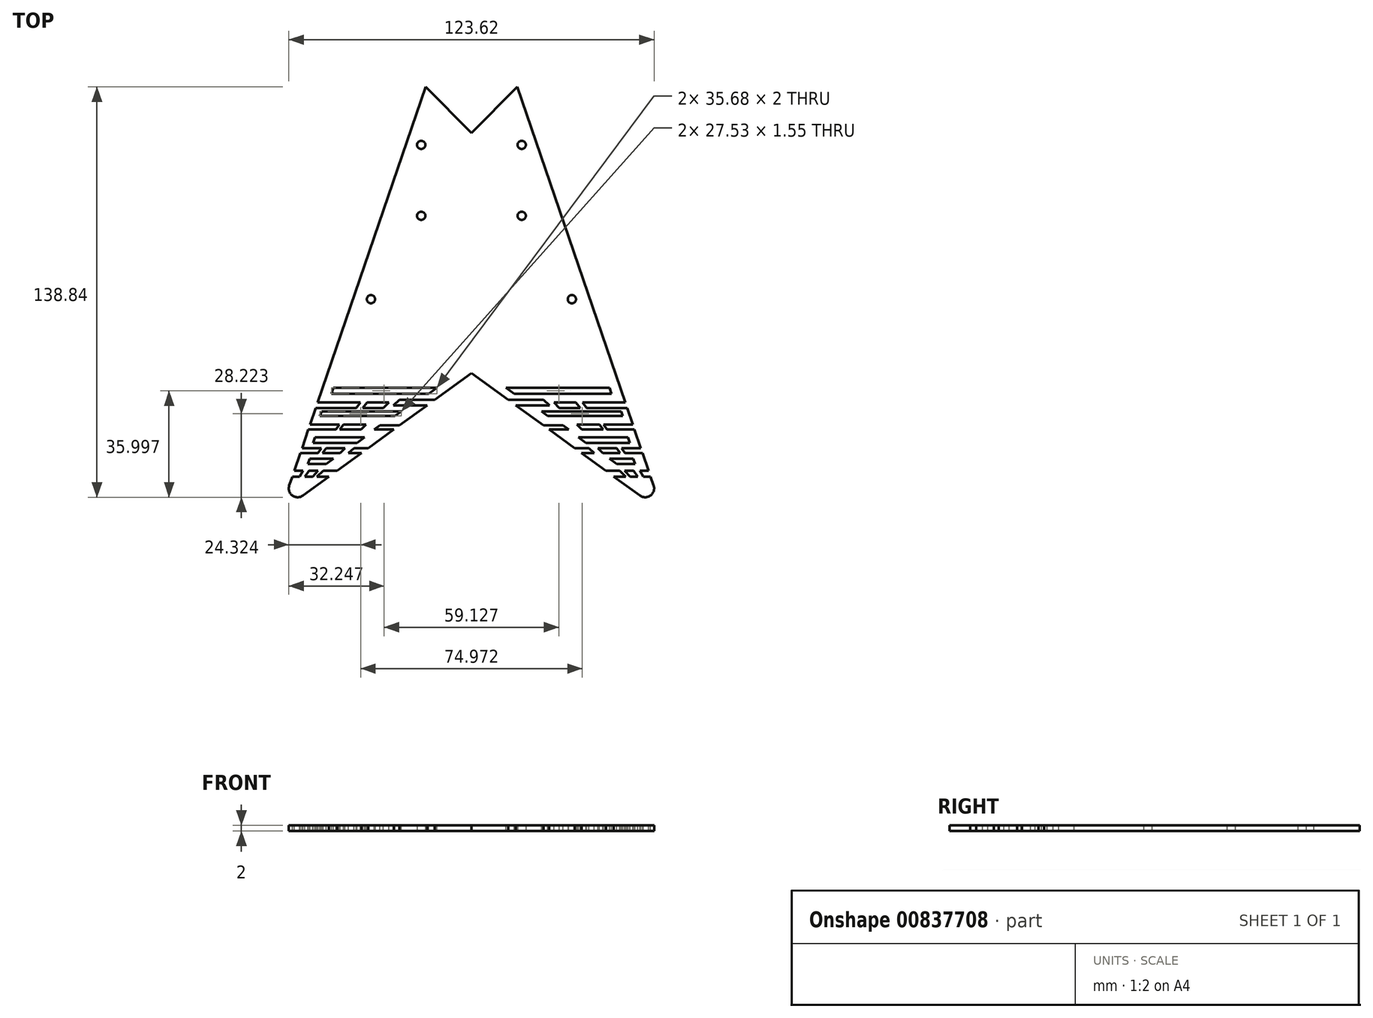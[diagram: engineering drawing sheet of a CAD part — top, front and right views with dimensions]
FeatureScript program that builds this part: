
annotation { "Feature Type Name" : "Feature", "Feature Type Description" : "" }
export const myFeature = defineFeature(function(context is Context, id is Id, definition is map)
    precondition{}
    {
        {
            var Q0;
            Q0=qCreatedBy(makeId("Top.planeOp"),FACE);
            var sketch = newSketch(context, id + "F0", { "sketchPlane" : qUnion([Q0])});
            skLineSegment(sketch, "E0", {"start": v(0, 142.22) * mm, "end": v(-64.72, -47.02) * mm});
            skLineSegment(sketch, "E1", {"start": v(-64.72, -47.02) * mm, "end": v(0, 0) * mm});
            skLineSegment(sketch, "E2.MirrorCS", {"start": v(0, 142.22) * mm, "end": v(64.72, -47.02) * mm});
            skLineSegment(sketch, "E3.MirrorCS", {"start": v(64.72, -47.02) * mm, "end": v(0, 0) * mm});
            skCircle(sketch, "E4", {"center": v(-17, 77.22) * mm, "radius": 1.4 * mm});
            skCircle(sketch, "E5", {"center": v(-17, 53.22) * mm, "radius": 1.4 * mm});
            skCircle(sketch, "E6.MirrorC", {"center": v(17, 77.22) * mm, "radius": 1.4 * mm});
            skCircle(sketch, "E7.MirrorC", {"center": v(17, 53.22) * mm, "radius": 1.4 * mm});
            skCircle(sketch, "E8", {"center": v(-34, 25) * mm, "radius": 1.4 * mm});
            skCircle(sketch, "E9.MirrorC", {"center": v(34, 25) * mm, "radius": 1.4 * mm});
            skSolve(sketch);
        }
        {
            var Q0;
            Q0 = qSketchRegion(id + "F0", true);
            extrude(context, id + "F1", {"entities" : qUnion([Q0]), "depth" : 2 * mm, "offsetDistance" : 25 * mm});
        }
        {
            var Q0;
            Q0=makeQuery(id+"F1.opExtrude","CAP_FACE",FACE,{"disambiguationData":[OSD([sQuery(id+"F0.wireOp",EDGE,"E0"),sQuery(id+"F0.wireOp",EDGE,"E1"),sQuery(id+"F0.wireOp",EDGE,"E2.MirrorCS"),sQuery(id+"F0.wireOp",EDGE,"E3.MirrorCS"),sQuery(id+"F0.wireOp",EDGE,"E4"),sQuery(id+"F0.wireOp",EDGE,"E5"),sQuery(id+"F0.wireOp",EDGE,"E6.MirrorC"),sQuery(id+"F0.wireOp",EDGE,"E7.MirrorC"),sQuery(id+"F0.wireOp",EDGE,"gKl59jUD-f7xt-qJ04-XvQ7-xEkOoHtsUVjT"),sQuery(id+"F0.wireOp",EDGE,"E8"),sQuery(id+"F0.wireOp",EDGE,"E9.MirrorC")])],"isStart":false});
            var sketch = newSketch(context, id + "F2", { "sketchPlane" : qUnion([Q0])});
            skLineSegment(sketch, "E10.bottom", {"start": v(-46.72, -5.02) * mm, "end": v(-11.72, -5.02) * mm});
            skLineSegment(sketch, "E11.bottom", {"start": v(-24.42, -9.02) * mm, "end": v(-12.42, -9.02) * mm});
            skLineSegment(sketch, "E12.bottom", {"start": v(-50.72, -13.02) * mm, "end": v(-23.72, -13.02) * mm});
            skLineSegment(sketch, "E13.bottom", {"start": v(-55.18, -19.11) * mm, "end": v(-45.87, -19.11) * mm});
            skLineSegment(sketch, "E14.bottom", {"start": v(-52.95, -21.77) * mm, "end": v(-36.18, -21.77) * mm});
            skLineSegment(sketch, "E15.bottom", {"start": v(-57.88, -27.02) * mm, "end": v(-51.93, -27.1) * mm});
            skLineSegment(sketch, "E16.bottom", {"start": v(-49.2, -25.4) * mm, "end": v(-42.82, -25.4) * mm});
            skLineSegment(sketch, "E17.bottom", {"start": v(-39.7, -25.4) * mm, "end": v(-34.96, -25.4) * mm});
            skLineSegment(sketch, "E18.bottom", {"start": v(-54.72, -29.02) * mm, "end": v(-46.72, -29.02) * mm});
            skLineSegment(sketch, "E19", {"start": v(-60.62, -35.02) * mm, "end": v(-59.93, -33.02) * mm});
            skLineSegment(sketch, "E20", {"start": v(-46.72, -5.02) * mm, "end": v(-47.4, -7.02) * mm});
            skLineSegment(sketch, "E21", {"start": v(-11.72, -5.02) * mm, "end": v(-14.47, -7.02) * mm});
            skLineSegment(sketch, "E22", {"start": v(-14.47, -7.02) * mm, "end": v(-47.4, -7.02) * mm});
            skLineSegment(sketch, "E23", {"start": v(-52.7, -11.87) * mm, "end": v(-52.05, -9.98) * mm});
            skLineSegment(sketch, "E24", {"start": v(-52.05, -9.98) * mm, "end": v(-37.59, -9.98) * mm});
            skLineSegment(sketch, "E25", {"start": v(-37.59, -9.98) * mm, "end": v(-38.97, -11.87) * mm});
            skLineSegment(sketch, "E26", {"start": v(-24.42, -9.02) * mm, "end": v(-26.42, -10.9) * mm});
            skLineSegment(sketch, "E27", {"start": v(-26.42, -10.9) * mm, "end": v(-15.02, -10.9) * mm});
            skLineSegment(sketch, "E28", {"start": v(-15.02, -10.9) * mm, "end": v(-12.42, -9.02) * mm});
            skLineSegment(sketch, "E29", {"start": v(-52.7, -11.87) * mm, "end": v(-38.97, -11.87) * mm});
            skLineSegment(sketch, "E30", {"start": v(-50.72, -13.02) * mm, "end": v(-51.25, -14.57) * mm});
            skLineSegment(sketch, "E31", {"start": v(-51.25, -14.57) * mm, "end": v(-25.85, -14.57) * mm});
            skLineSegment(sketch, "E32", {"start": v(-25.85, -14.57) * mm, "end": v(-23.72, -13.02) * mm});
            skLineSegment(sketch, "E33", {"start": v(-54.6, -17.46) * mm, "end": v(-44.75, -17.46) * mm});
            skLineSegment(sketch, "E34", {"start": v(-44.75, -17.46) * mm, "end": v(-45.87, -19.11) * mm});
            skLineSegment(sketch, "E35", {"start": v(-26.3, -19.11) * mm, "end": v(-24.37, -17.7) * mm});
            skLineSegment(sketch, "E36", {"start": v(-43.33, -17.44) * mm, "end": v(-35.64, -17.44) * mm});
            skLineSegment(sketch, "E37", {"start": v(-35.64, -17.44) * mm, "end": v(-37.29, -19.11) * mm});
            skLineSegment(sketch, "E38", {"start": v(-37.29, -19.11) * mm, "end": v(-44.54, -19.11) * mm});
            skLineSegment(sketch, "E39", {"start": v(-44.54, -19.11) * mm, "end": v(-43.33, -17.44) * mm});
            skLineSegment(sketch, "E40", {"start": v(-52.95, -21.77) * mm, "end": v(-53.6, -23.66) * mm});
            skLineSegment(sketch, "E41", {"start": v(-53.6, -23.66) * mm, "end": v(-38.79, -23.66) * mm});
            skLineSegment(sketch, "E42", {"start": v(-38.79, -23.66) * mm, "end": v(-36.18, -21.77) * mm});
            skLineSegment(sketch, "E43", {"start": v(-57.88, -27.02) * mm, "end": v(-57.33, -25.4) * mm});
            skLineSegment(sketch, "E44", {"start": v(-57.33, -25.4) * mm, "end": v(-50.84, -25.4) * mm});
            skLineSegment(sketch, "E45", {"start": v(-50.84, -25.4) * mm, "end": v(-51.93, -27.1) * mm});
            skLineSegment(sketch, "E46", {"start": v(-49.2, -25.4) * mm, "end": v(-50.36, -27.02) * mm});
            skLineSegment(sketch, "E47", {"start": v(-50.36, -27.02) * mm, "end": v(-44.46, -27.02) * mm});
            skLineSegment(sketch, "E48", {"start": v(-44.46, -27.02) * mm, "end": v(-42.82, -25.4) * mm});
            skLineSegment(sketch, "E49", {"start": v(-39.7, -25.4) * mm, "end": v(-41.58, -27.02) * mm});
            skLineSegment(sketch, "E50", {"start": v(-41.58, -27.02) * mm, "end": v(-37.2, -27.02) * mm});
            skLineSegment(sketch, "E51", {"start": v(-37.2, -27.02) * mm, "end": v(-34.96, -25.4) * mm});
            skLineSegment(sketch, "E52", {"start": v(-54.72, -29.02) * mm, "end": v(-55.33, -30.8) * mm});
            skLineSegment(sketch, "E53", {"start": v(-55.33, -30.8) * mm, "end": v(-49.18, -30.8) * mm});
            skLineSegment(sketch, "E54", {"start": v(-49.18, -30.8) * mm, "end": v(-46.72, -29.02) * mm});
            skLineSegment(sketch, "E55", {"start": v(-31, -17.7) * mm, "end": v(-32.95, -19.11) * mm});
            skLineSegment(sketch, "E56", {"start": v(-32.95, -19.11) * mm, "end": v(-26.3, -19.11) * mm});
            skLineSegment(sketch, "E57", {"start": v(-31, -17.7) * mm, "end": v(-24.37, -17.7) * mm});
            skLineSegment(sketch, "E58", {"start": v(-59.93, -33.02) * mm, "end": v(-57.06, -33.02) * mm});
            skLineSegment(sketch, "E59", {"start": v(-57.06, -33.02) * mm, "end": v(-58.16, -35.02) * mm});
            skLineSegment(sketch, "E60", {"start": v(-58.16, -35.02) * mm, "end": v(-60.62, -35.02) * mm});
            skLineSegment(sketch, "E61", {"start": v(-54.94, -33.02) * mm, "end": v(-51.89, -33.02) * mm});
            skLineSegment(sketch, "E62", {"start": v(-51.89, -33.02) * mm, "end": v(-53.7, -35.02) * mm});
            skLineSegment(sketch, "E63", {"start": v(-53.7, -35.02) * mm, "end": v(-56.33, -35.02) * mm});
            skLineSegment(sketch, "E64", {"start": v(-50.19, -33.02) * mm, "end": v(-45.45, -33.02) * mm});
            skLineSegment(sketch, "E65", {"start": v(-45.45, -33.02) * mm, "end": v(-48.2, -35.02) * mm});
            skLineSegment(sketch, "E66", {"start": v(-48.2, -35.02) * mm, "end": v(-52.26, -35.02) * mm});
            skLineSegment(sketch, "E67", {"start": v(-54.94, -33.02) * mm, "end": v(-56.33, -35.02) * mm});
            skLineSegment(sketch, "E68", {"start": v(-50.19, -33.02) * mm, "end": v(-52.26, -35.02) * mm});
            skLineSegment(sketch, "E69", {"start": v(-35.35, -9.98) * mm, "end": v(-36.85, -11.87) * mm});
            skLineSegment(sketch, "E70", {"start": v(-36.85, -11.87) * mm, "end": v(-29.78, -11.87) * mm});
            skLineSegment(sketch, "E71", {"start": v(-29.78, -11.87) * mm, "end": v(-27.9, -9.98) * mm});
            skLineSegment(sketch, "E72", {"start": v(-27.9, -9.98) * mm, "end": v(-35.35, -9.98) * mm});
            skLineSegment(sketch, "E73", {"start": v(-55.18, -19.11) * mm, "end": v(-54.6, -17.46) * mm});
            skLineSegment(sketch, "E74.MirrorCS", {"start": v(26.3, -19.11) * mm, "end": v(24.37, -17.7) * mm});
            skLineSegment(sketch, "E75.MirrorCS", {"start": v(49.18, -30.8) * mm, "end": v(46.72, -29.02) * mm});
            skLineSegment(sketch, "E76.MirrorCS", {"start": v(44.75, -17.46) * mm, "end": v(45.87, -19.11) * mm});
            skLineSegment(sketch, "E77.MirrorCS", {"start": v(52.95, -21.77) * mm, "end": v(53.6, -23.66) * mm});
            skLineSegment(sketch, "E78.MirrorCS", {"start": v(38.79, -23.66) * mm, "end": v(36.18, -21.77) * mm});
            skLineSegment(sketch, "E79.MirrorCS", {"start": v(57.88, -27.02) * mm, "end": v(57.33, -25.4) * mm});
            skLineSegment(sketch, "E80.MirrorCS", {"start": v(53.7, -35.02) * mm, "end": v(56.33, -35.02) * mm});
            skLineSegment(sketch, "E81.MirrorCS", {"start": v(37.2, -27.02) * mm, "end": v(34.96, -25.4) * mm});
            skLineSegment(sketch, "E82.MirrorCS", {"start": v(45.45, -33.02) * mm, "end": v(48.2, -35.02) * mm});
            skLineSegment(sketch, "E83.MirrorCS", {"start": v(24.42, -9.02) * mm, "end": v(26.42, -10.9) * mm});
            skLineSegment(sketch, "E84.MirrorCS", {"start": v(50.36, -27.02) * mm, "end": v(44.46, -27.02) * mm});
            skLineSegment(sketch, "E85.MirrorCS", {"start": v(44.46, -27.02) * mm, "end": v(42.82, -25.4) * mm});
            skLineSegment(sketch, "E86.MirrorCS", {"start": v(35.35, -9.98) * mm, "end": v(36.85, -11.87) * mm});
            skLineSegment(sketch, "E87.MirrorCS", {"start": v(39.7, -25.4) * mm, "end": v(34.96, -25.4) * mm});
            skLineSegment(sketch, "E88.MirrorCS", {"start": v(54.72, -29.02) * mm, "end": v(55.33, -30.8) * mm});
            skLineSegment(sketch, "E89.MirrorCS", {"start": v(31, -17.7) * mm, "end": v(32.95, -19.11) * mm});
            skLineSegment(sketch, "E90.MirrorCS", {"start": v(15.02, -10.9) * mm, "end": v(12.42, -9.02) * mm});
            skLineSegment(sketch, "E91.MirrorCS", {"start": v(54.94, -33.02) * mm, "end": v(56.33, -35.02) * mm});
            skLineSegment(sketch, "E92.MirrorCS", {"start": v(37.59, -9.98) * mm, "end": v(38.97, -11.87) * mm});
            skLineSegment(sketch, "E93.MirrorCS", {"start": v(35.64, -17.44) * mm, "end": v(37.29, -19.11) * mm});
            skLineSegment(sketch, "E94.MirrorCS", {"start": v(50.19, -33.02) * mm, "end": v(52.26, -35.02) * mm});
            skLineSegment(sketch, "E95.MirrorCS", {"start": v(54.72, -29.02) * mm, "end": v(46.72, -29.02) * mm});
            skLineSegment(sketch, "E96.MirrorCS", {"start": v(46.72, -5.02) * mm, "end": v(47.4, -7.02) * mm});
            skLineSegment(sketch, "E97.MirrorCS", {"start": v(57.33, -25.4) * mm, "end": v(50.84, -25.4) * mm});
            skLineSegment(sketch, "E98.MirrorCS", {"start": v(50.72, -13.02) * mm, "end": v(51.25, -14.57) * mm});
            skLineSegment(sketch, "E99.MirrorCS", {"start": v(55.33, -30.8) * mm, "end": v(49.18, -30.8) * mm});
            skLineSegment(sketch, "E100.MirrorCS", {"start": v(55.18, -19.11) * mm, "end": v(54.6, -17.46) * mm});
            skLineSegment(sketch, "E101.MirrorCS", {"start": v(48.2, -35.02) * mm, "end": v(52.26, -35.02) * mm});
            skLineSegment(sketch, "E102.MirrorCS", {"start": v(49.2, -25.4) * mm, "end": v(50.36, -27.02) * mm});
            skLineSegment(sketch, "E103.MirrorCS", {"start": v(25.85, -14.57) * mm, "end": v(23.72, -13.02) * mm});
            skLineSegment(sketch, "E104.MirrorCS", {"start": v(39.7, -25.4) * mm, "end": v(41.58, -27.02) * mm});
            skLineSegment(sketch, "E105.MirrorCS", {"start": v(51.89, -33.02) * mm, "end": v(53.7, -35.02) * mm});
            skLineSegment(sketch, "E106.MirrorCS", {"start": v(50.84, -25.4) * mm, "end": v(51.93, -27.1) * mm});
            skLineSegment(sketch, "E107.MirrorCS", {"start": v(44.54, -19.11) * mm, "end": v(43.33, -17.44) * mm});
            skLineSegment(sketch, "E108.MirrorCS", {"start": v(54.94, -33.02) * mm, "end": v(51.89, -33.02) * mm});
            skLineSegment(sketch, "E109.MirrorCS", {"start": v(50.19, -33.02) * mm, "end": v(45.45, -33.02) * mm});
            skLineSegment(sketch, "E110.MirrorCS", {"start": v(41.58, -27.02) * mm, "end": v(37.2, -27.02) * mm});
            skLineSegment(sketch, "E111.MirrorCS", {"start": v(52.7, -11.87) * mm, "end": v(52.05, -9.98) * mm});
            skLineSegment(sketch, "E112.MirrorCS", {"start": v(57.88, -27.02) * mm, "end": v(51.93, -27.1) * mm});
            skLineSegment(sketch, "E113.MirrorCS", {"start": v(29.78, -11.87) * mm, "end": v(27.9, -9.98) * mm});
            skLineSegment(sketch, "E114.MirrorCS", {"start": v(36.85, -11.87) * mm, "end": v(29.78, -11.87) * mm});
            skLineSegment(sketch, "E115.MirrorCS", {"start": v(32.95, -19.11) * mm, "end": v(26.3, -19.11) * mm});
            skLineSegment(sketch, "E116.MirrorCS", {"start": v(50.72, -13.02) * mm, "end": v(23.72, -13.02) * mm});
            skLineSegment(sketch, "E117.MirrorCS", {"start": v(49.2, -25.4) * mm, "end": v(42.82, -25.4) * mm});
            skLineSegment(sketch, "E118.MirrorCS", {"start": v(14.47, -7.02) * mm, "end": v(47.4, -7.02) * mm});
            skLineSegment(sketch, "E119.MirrorCS", {"start": v(26.42, -10.9) * mm, "end": v(15.02, -10.9) * mm});
            skLineSegment(sketch, "E120.MirrorCS", {"start": v(53.6, -23.66) * mm, "end": v(38.79, -23.66) * mm});
            skLineSegment(sketch, "E121.MirrorCS", {"start": v(27.9, -9.98) * mm, "end": v(35.35, -9.98) * mm});
            skLineSegment(sketch, "E122.MirrorCS", {"start": v(54.6, -17.46) * mm, "end": v(44.75, -17.46) * mm});
            skLineSegment(sketch, "E123.MirrorCS", {"start": v(31, -17.7) * mm, "end": v(24.37, -17.7) * mm});
            skLineSegment(sketch, "E124.MirrorCS", {"start": v(52.05, -9.98) * mm, "end": v(37.59, -9.98) * mm});
            skLineSegment(sketch, "E125.MirrorCS", {"start": v(52.95, -21.77) * mm, "end": v(36.18, -21.77) * mm});
            skLineSegment(sketch, "E126.MirrorCS", {"start": v(37.29, -19.11) * mm, "end": v(44.54, -19.11) * mm});
            skLineSegment(sketch, "E127.MirrorCS", {"start": v(43.33, -17.44) * mm, "end": v(35.64, -17.44) * mm});
            skLineSegment(sketch, "E128.MirrorCS", {"start": v(24.42, -9.02) * mm, "end": v(12.42, -9.02) * mm});
            skLineSegment(sketch, "E129.MirrorCS", {"start": v(55.18, -19.11) * mm, "end": v(45.87, -19.11) * mm});
            skLineSegment(sketch, "E130.MirrorCS", {"start": v(52.7, -11.87) * mm, "end": v(38.97, -11.87) * mm});
            skLineSegment(sketch, "E131.MirrorCS", {"start": v(51.25, -14.57) * mm, "end": v(25.85, -14.57) * mm});
            skLineSegment(sketch, "E132.MirrorCS", {"start": v(59.93, -33.02) * mm, "end": v(57.06, -33.02) * mm});
            skLineSegment(sketch, "E133.MirrorCS", {"start": v(58.16, -35.02) * mm, "end": v(60.62, -35.02) * mm});
            skLineSegment(sketch, "E134.MirrorCS", {"start": v(57.06, -33.02) * mm, "end": v(58.16, -35.02) * mm});
            skLineSegment(sketch, "E135.MirrorCS", {"start": v(60.62, -35.02) * mm, "end": v(59.93, -33.02) * mm});
            skLineSegment(sketch, "E136.MirrorCS", {"start": v(11.72, -5.02) * mm, "end": v(14.47, -7.02) * mm});
            skLineSegment(sketch, "E137.MirrorCS", {"start": v(46.72, -5.02) * mm, "end": v(11.72, -5.02) * mm});
            skSolve(sketch);
        }
        {
            var Q0;
            Q0 = qSketchRegion(id + "F2", true);
            extrude(context, id + "F3", {"entities" : qUnion([Q0]), "operationType" : NewBodyOperationType.REMOVE, "endBound" : BoundingType.THROUGH_ALL, "oppositeDirection" : true, "depth" : 25 * mm, "offsetDistance" : 25 * mm});
        }
        {
            var Q0;
            Q0=makeQuery(id+"F1.opExtrude","SWEPT_EDGE",EDGE,{"disambiguationData":[OSD([sQuery(id+"F0.wireOp",EDGE,"E0"),sQuery(id+"F0.wireOp",EDGE,"E1")])]});
            fillet(context, id + "F4", {"entities" : qUnion([Q0]), "radius" : 3 * mm, "tangentPropagation" : true, "allowEdgeOverflow" : false});
        }
        {
            var Q0;
            Q0=makeQuery(id+"F1.opExtrude","SWEPT_EDGE",EDGE,{"disambiguationData":[OSD([sQuery(id+"F0.wireOp",EDGE,"E2.MirrorCS"),sQuery(id+"F0.wireOp",EDGE,"E3.MirrorCS")])]});
            fillet(context, id + "F5", {"entities" : qUnion([Q0]), "radius" : 3 * mm, "tangentPropagation" : true, "allowEdgeOverflow" : false});
        }
        {
            var Q0;
            Q0=makeQuery(id+"F1.opExtrude","CAP_FACE",FACE,{"disambiguationData":[OSD([sQuery(id+"F0.wireOp",EDGE,"E0"),sQuery(id+"F0.wireOp",EDGE,"E1"),sQuery(id+"F0.wireOp",EDGE,"E2.MirrorCS"),sQuery(id+"F0.wireOp",EDGE,"E3.MirrorCS"),sQuery(id+"F0.wireOp",EDGE,"E4"),sQuery(id+"F0.wireOp",EDGE,"E5"),sQuery(id+"F0.wireOp",EDGE,"E6.MirrorC"),sQuery(id+"F0.wireOp",EDGE,"E7.MirrorC"),sQuery(id+"F0.wireOp",EDGE,"E8"),sQuery(id+"F0.wireOp",EDGE,"E9.MirrorC")])],"isStart":false});
            var sketch = newSketch(context, id + "F6", { "sketchPlane" : qUnion([Q0])});
            skLineSegment(sketch, "E138", {"start": v(0, 81.27) * mm, "end": v(-15.53, 96.82) * mm});
            skLineSegment(sketch, "E139", {"start": v(-15.53, 96.82) * mm, "end": v(0, 142.22) * mm});
            skLineSegment(sketch, "E140", {"start": v(0, 142.22) * mm, "end": v(15.53, 96.82) * mm});
            skLineSegment(sketch, "E141", {"start": v(15.53, 96.82) * mm, "end": v(0, 81.27) * mm});
            skSolve(sketch);
        }
        {
            var Q0;
            Q0 = qSketchRegion(id + "F6", true);
            extrude(context, id + "F7", {"entities" : qUnion([Q0]), "operationType" : NewBodyOperationType.REMOVE, "endBound" : BoundingType.THROUGH_ALL, "oppositeDirection" : true, "depth" : 25 * mm, "offsetDistance" : 25 * mm});
        }
    });
